# Revit family: Faucet-Lavatory-American_Standard-Estate-7722.801
name_source: partatom
category: Plumbing Fixtures
revit_build: Autodesk Revit 2014 (Build: 20130308_1515(x64)
units: mm (PartAtom-declared; Revit-internal decimal feet)

## types (1)
- 7722.801
    ADA Compliant = Yes
    Assembly Code = D2020300
    CW Connection = No
    CWFU = 0
    Cold Water Connection Diameter = 3/8"
    Cold Water Connection Radius = 3/16"
    Cold Water Connection Width = 4"
    Default Elevation = 0"
    Description = Estate Widespread Bathroom Sink Faucet
    Finish = Brass-American Standard-002-Polished Chrome
    Flow Rate = 1.2 gpm (4.5 L/min)
    HW Connection = No
    HWFU = 0
    Height = 7 5/8"
    Hot Water Connection Diameter = 0"
    Hot Water Connection Radius = 3/16"
    Hot Water Connection Width = 4"
    Installation Type = Deck Mounted
    Length = 6"
    Manufacturer = American Standard
    Material = Brass-American Standard-002-Polished Chrome
    Model = 7722.801
    Price = Prices may vary. Please consult Manufacturer Representative for most up-to-date price list.
    Product Documentation Link = https://www.americanstandard-us.com
    Product Page URL = https://www.americanstandard-us.com
    URL = https://www.americanstandard-us.com
    Vent Connection = No
    Warranty Information = Limited Lifetime Warranty
    Waste Connection = No
    Width = 14"

## geometry (parser evidence)
native form markers: Sweep x1
no freeform markers — native parametric forms only
